# Revit family: Electrical_Equipment-Floor_Box-Hubbell_Wiring-11_Gang-CFB11G_Series
name_source: partatom
category: Electrical Fixtures
revit_build: Autodesk Revit 2015 (Build: 20140606_1530(x64)
units: mm (PartAtom-declared; Revit-internal decimal feet)

## types (2) — shared parameters
Assembly Code = D5020115
Box Material = Metal-Hubbell-Stamped Steel
Conduit Connector 1 Radius = 0' - 0 1/2"
Conduit Connector 2 Radius = 0' - 0 5/8"
Conduit Connector 3 Radius = 0' - 0 3/4"
Conduit Connector 4 Radius = 0' - 1"
Conduit Connector_1 Description = Conduit 1.25in or 1.0in Connection
Conduit Connector_10 Description = Conduit 1.5in, 1.25in or 1.0in Connection
Conduit Connector_11 Description = Conduit 2.0in Connection
Conduit Connector_12 Description = Conduit 1.5in, 1.25in or 1.0in Connection
Conduit Connector_13 Description = Conduit 1.5in, 1.25in or 1.0in Connection
Conduit Connector_14 Description = Conduit 1.0in or 0.75in Connection
Conduit Connector_15 Description = Conduit 1.0in or 0.75in Connection
Conduit Connector_16 Description = Conduit 1.5in, 1.25in or 1.0in Connection
Conduit Connector_17 Description = Conduit 1.5in, 1.25in or 1.0in Connection
Conduit Connector_18 Description = Conduit 1.5in, 1.25in or 1.0in Connection
Conduit Connector_2 Description = Conduit 1.25in or 1.0in Connection
Conduit Connector_3 Description = Conduit 1.5in, 1.25in or 1.0in Connection
Conduit Connector_4 Description = Conduit 1.5in, 1.25in or 1.0in Connection
Conduit Connector_5 Description = Conduit 1.0in or 0.75in Connection
Conduit Connector_6 Description = Conduit 1.0in or 0.75in Connection
Conduit Connector_7 Description = Conduit 1.25in or 1.0in Connection
Conduit Connector_8 Description = Conduit 1.25in or 1.0in Connection
Conduit Connector_9 Description = Conduit 1.5in, 1.25in or 1.0in Connection
Default Elevation = 0' - 0"
Description = Recessed Stamped Steel Concrete Floor Box
Manufacturer = Hubbell-Wiring
Product Documentation Link = http://ecatalog.hubbell-wiring.com
Product Page URL = http://ecatalog.hubbell-wiring.com
Product data url = https://bimobject.com
URL = http://www.hubbell-wiring.com

## per-type parameters (varying)
| type | Floor Box Type | Model |
| CFB11G4 - 11 Gang - Stamped Steel | Recessed Concrete Floor Box : CFB11G4 - Recessed Concrete Floor Box - Stamped Steel | CFB11G4 |
| CFB11G6 - 11 Gang - Stamped Steel | Recessed Concrete Floor Box : CFB11G6 - Recessed Concrete Floor Box - Stamped Steel | CFB11G6 |

## geometry (parser evidence)
native form markers: Blend x10, Sweep x7
no freeform markers — native parametric forms only
